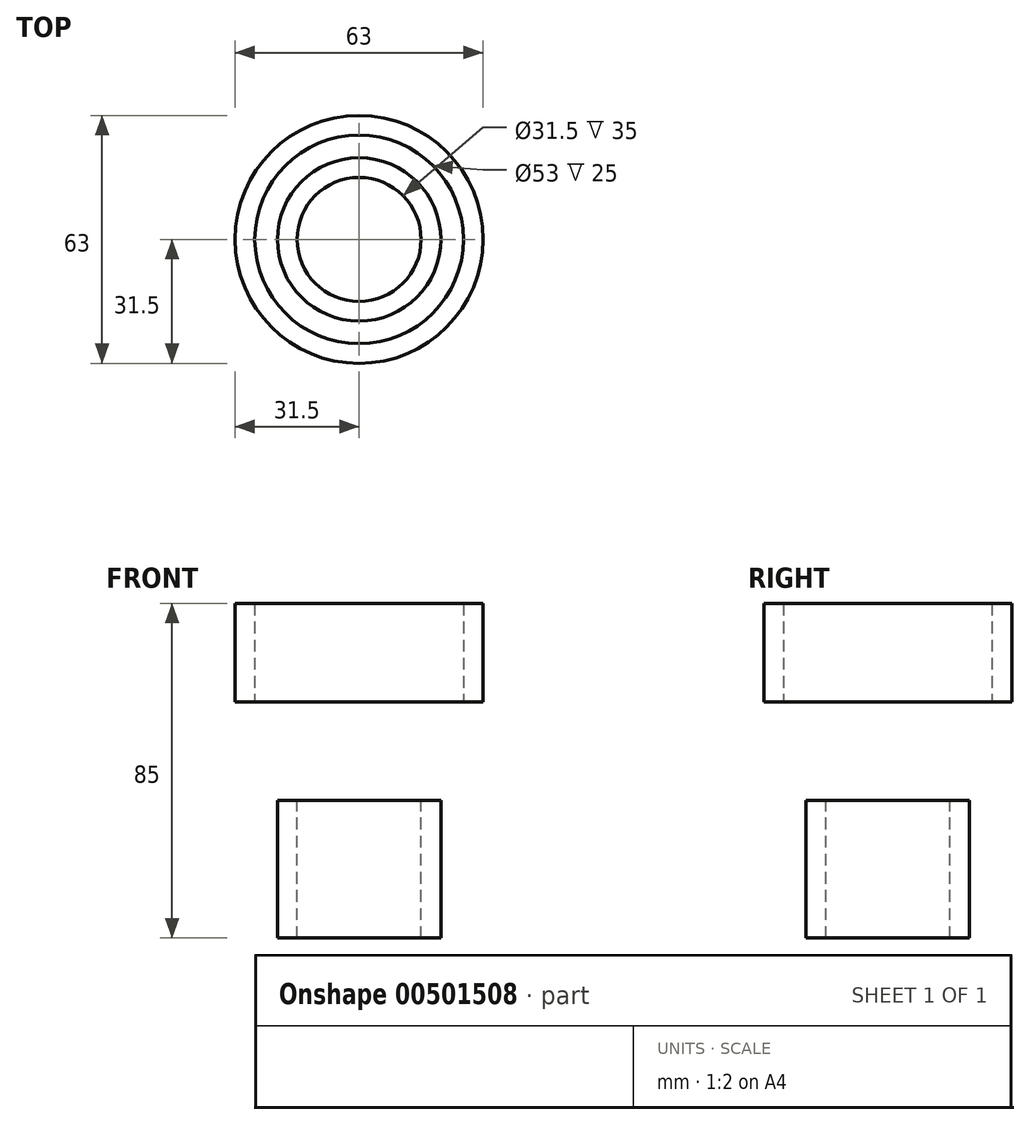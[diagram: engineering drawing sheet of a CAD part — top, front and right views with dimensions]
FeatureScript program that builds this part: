
annotation { "Feature Type Name" : "Feature", "Feature Type Description" : "" }
export const myFeature = defineFeature(function(context is Context, id is Id, definition is map)
    precondition{}
    {
        {
            var Q0;
            Q0=qCreatedBy(makeId("Top.planeOp"),FACE);
            var sketch = newSketch(context, id + "F0", { "sketchPlane" : qUnion([Q0])});
            skCircle(sketch, "E0", {"center": v(0, 0) * mm, "radius": 15.75 * mm});
            skCircle(sketch, "E1.0", {"center": v(0, 0) * mm, "radius": 20.75 * mm});
            skSolve(sketch);
        }
        {
            var Q0;
            Q0=qCreatedBy(makeId("Top.planeOp"),FACE);
            cPlane(context, id + "F1", {"entities" : qUnion([Q0]), "cplaneType" : CPlaneType.OFFSET, "offset" : 25 * mm, "width" : 150 * mm, "height" : 150 * mm});
        }
        {
            var Q0;
            Q0=qCreatedBy(id+"F1.planeOp",FACE);
            var sketch = newSketch(context, id + "F2", { "sketchPlane" : qUnion([Q0])});
            skCircle(sketch, "E2", {"center": v(0, 0) * mm, "radius": 26.5 * mm});
            skCircle(sketch, "E3.0", {"center": v(0, 0) * mm, "radius": 31.5 * mm});
            skSolve(sketch);
        }
        {
            var Q0;
            Q0=makeQuery(id+"F0.imprint","IMPRINT",FACE,{"disambiguationData":[TD([[makeQuery(id+"F0.imprint","IMPRINT",EDGE,{"derivedFrom":sQuery(id+"F0.wireOp",EDGE,"E0")}),-1.0]])]});
            extrude(context, id + "F3", {"entities" : qUnion([Q0]), "oppositeDirection" : true, "depth" : 35 * mm});
        }
        {
            var Q0;
            Q0=makeQuery(id+"F2.imprint","IMPRINT",FACE,{"disambiguationData":[TD([[makeQuery(id+"F2.imprint","IMPRINT",EDGE,{"derivedFrom":sQuery(id+"F2.wireOp",EDGE,"E2")}),-1.0]])]});
            extrude(context, id + "F4", {"entities" : qUnion([Q0]), "depth" : 25 * mm});
        }
        {
            var Q0;
            Q0=makeQuery(id+"F3.opExtrude","CAP_EDGE",EDGE,{"disambiguationData":[OSD([sQuery(id+"F0.wireOp",EDGE,"E0")])],"isStart":true});
            var Q1;
            Q1=makeQuery(id+"F4.opExtrude","CAP_EDGE",EDGE,{"disambiguationData":[OSD([sQuery(id+"F2.wireOp",EDGE,"E2")])],"isStart":true});
            loft(context, id + "F5", {"bodyType" : ToolBodyType.SURFACE, "wireProfilesArray" : [{ "wireProfileEntities" : qUnion([Q0]) }, { "wireProfileEntities" : qUnion([Q1]) }]});
        }
        {
            var Q0;
            Q0=makeQuery(id+"F4.opExtrude","CAP_EDGE",EDGE,{"disambiguationData":[OSD([sQuery(id+"F2.wireOp",EDGE,"E3.0")])],"isStart":true});
            var Q1;
            Q1=makeQuery(id+"F3.opExtrude","CAP_EDGE",EDGE,{"disambiguationData":[OSD([sQuery(id+"F0.wireOp",EDGE,"E1.0")])],"isStart":true});
            loft(context, id + "F6", {"bodyType" : ToolBodyType.SURFACE, "wireProfilesArray" : [{ "wireProfileEntities" : qUnion([Q0]) }, { "wireProfileEntities" : qUnion([Q1]) }]});
        }
    });
